# Revit family: TOP HYBRID PLUS
name_source: partatom
category: Attrezzatura meccanica
units: mm (PartAtom-declared; Revit-internal decimal feet)

## family parameters
Basato su piano di lavoro = No
Classificazione = Nessuno
Condiviso = No
Mantieni orientamento annotazione = No
Punto di calcolo locali = No
Quota connettore circolare = Usa diametro
Sempre verticale = Sì
Taglio con vuoti quando caricato = No
Tipo di parte = Normale

## types (1)
- TOP HYBRID PLUS
    Date of publishing = 03/05/2024
    Depth = 350 mm  [stored 1.14829 ft]
    Domestic Cold Water Diameter = 21 mm  [stored 0.0688976 ft]
    Domestic Hot Water Diameter = 21 mm  [stored 0.0688976 ft]
    Efficiency 30% = 105,60%
    Flue outlet = 80 mm  [stored 0.262467 ft]
    Gas Inlet Diameter = 26 mm
    Height = 1415 mm  [stored 4.64239 ft]
    Hydronic Return Diameter = 26 mm
    Hydronic Supply Diameter = 26 mm
    Manufacturer country = Italy
    Manufacturer name = Italtherm S.p.A.
    Material main = Metal
    Material secondary = Plastic
    Maximum heat output 50/30°C = 34800 W
    Maximum heat output 80/60°C = 32200 W
    Maximum heating heat input = 33000 W
    Maximum sanitary pressure = 6 bar
    Maximum system pressure = 3 bar
    Minimum heat output 50/30°C = 1700 W
    Minimum heat output 80/60°C = 1500 W
    Nominal efficiency 50/30°C = 105,10%
    Nominal efficiency 80/60°C = 97,10%
    Power consumption (W) = 120 W
    Power supply | Frequency (Hz) = 50 Hz
    Power supply | Phase = 1
    Power supply | Voltage (V) = 230 V
    Prospetto di default = 0 mm  [stored 0 ft]
    Refrigerant Gas = 16 mm  [stored 0.0524934 ft]
    Siphon with condensate drain = 32 mm  [stored 0.104987 ft]
    Weight = 113,30 kg
    Width = 945 mm  [stored 3.10039 ft]

note: [stored X ft] marks values corroborated as IEEE doubles in the binary element streams (Revit-internal decimal feet)
